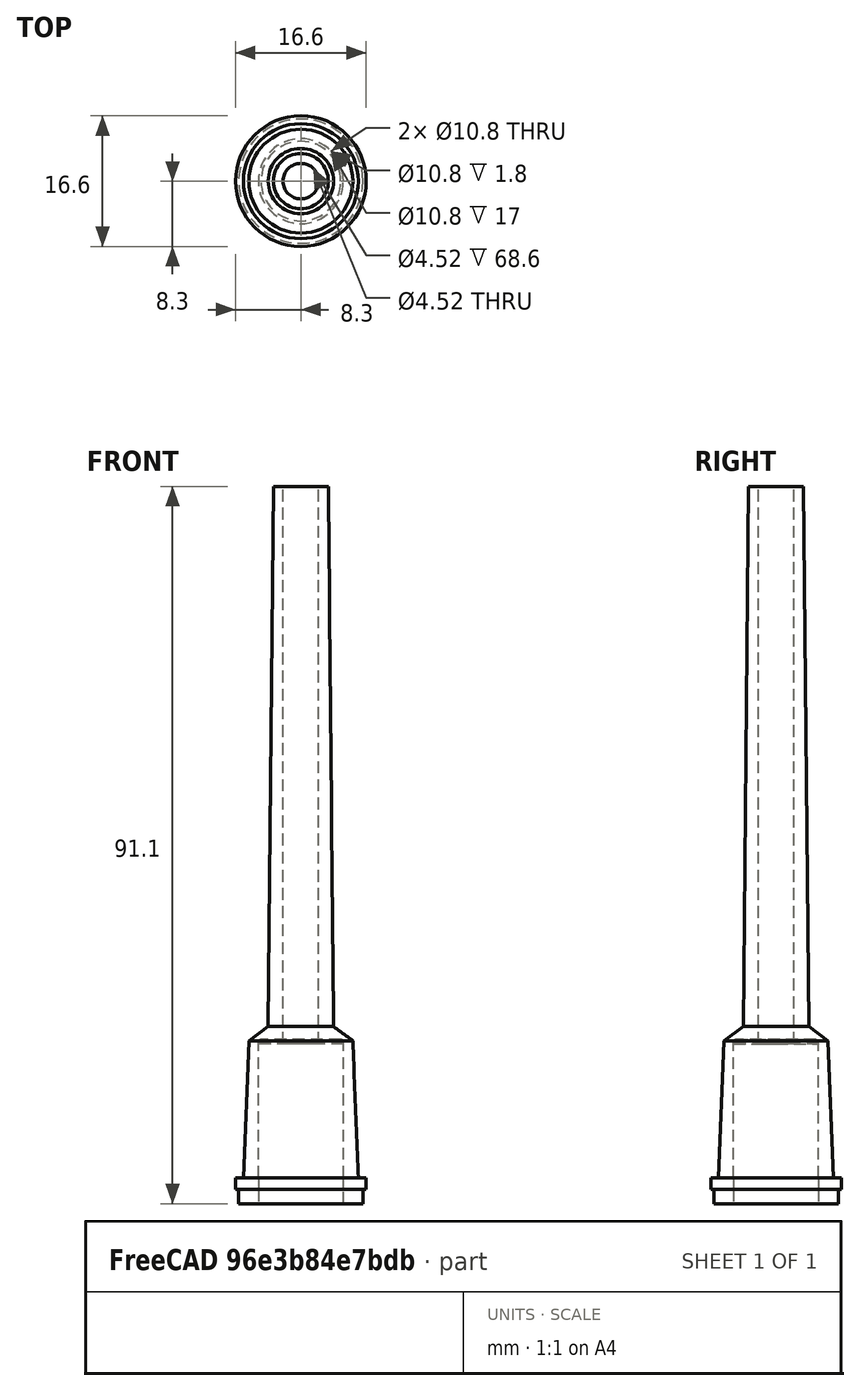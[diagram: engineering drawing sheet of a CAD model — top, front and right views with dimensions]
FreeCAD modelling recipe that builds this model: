
FCSTD DOCUMENT  (FreeCAD 0.19R17331 (Git))
Label: gilson_p200_vastago
License: All rights reserved
LicenseURL: http://en.wikipedia.org/wiki/All_rights_reserved
objects: Sketcher::SketchObject×9, PartDesign::AdditiveLoft×3, PartDesign::Pad×2, Spreadsheet::Sheet×1, App::FeaturePython×1, App::AnnotationLabel×1, PartDesign::Body×1
note: 20 computed .brp shape members not serialized (recipe doc carries the construction recipe); baked Part::Feature solids carry a one-line shape summary decoded from their .brp

FEATURE [Sketcher::SketchObject] Sketch  label="etapa1"
  MapMode = 5
  Support = -> [XY_Plane]
  expr: Constraints[3] = Spreadsheet.F2
  expr: Constraints[1] = Spreadsheet.B1
  sketch-geometry (2):
    g0: Circle CenterX=0 CenterY=0 CenterZ=0 NormalX=0 NormalY=0 NormalZ=1 AngleXU=0 Radius=7.9
    g1: Circle CenterX=0 CenterY=0 CenterZ=0 NormalX=0 NormalY=0 NormalZ=1 AngleXU=0 Radius=5.4
  constraints (4):
    c: Coincident(g0,g-1)
    c: Diameter(g0) = 15.8
    c: Coincident(g1,g0)
    c: Diameter(g1) = 10.8
FEATURE [PartDesign::Pad] Pad  label="etapa1pad"
  Length = 1.8
  Length2 = 100
  Profile = -> Sketch
  Type = 0
  expr: Length = Spreadsheet.B2
FEATURE [Spreadsheet::Sheet] Spreadsheet
  cells = A1=d1; B1=15.8; E1=h hueco interno; F1=20.3; A2=a1; B2=1.8; C2=cno reborde 45º; E2=d hueco interno; F2=10.8; G2=quizas 10.7; H2=parece ser cilindrico; E3=suma alturas externas; F3==B2 + B5 + B9 + B13; A4=d2; B4=16.6; A5=a2; B5=1.5; C5=altura cumul; D5==B2 + B5; G6=d piston; H6=4.02; A7=cono d1; B7=14.6; G7=tolerancia; H7==H6 + 0.5; A8=cono d2; B8=13.2; G8=h piston relajado; H8=49.2; A9=cono h; B9=17.4; C9=altura cumul; D9==D5 + B9; G9=desplazamiento max; H9==I9 - J9; I9=34.2; J9=14.8; G10=h piston maxima; H10==H8 + H9; A11=conito d1; B11==B8; A12=conito d2; B12=8.300000000000001; A13=conito h; B13=1.8; C13=altura cumul; D13==D9 + B13; A15=vastago h1; B15==90 - B18; C15=altura cumul; D15==D13 + B15; A16=vastago d1; B16==B12; A17=vastago d2; B17=5; C17=a la altura del desplazamiento maximo del piston es:; D17=7; A18=vastago h2; B18=0.8; A19=vastago d3; B19=4.5
FEATURE [Sketcher::SketchObject] Sketch001  label="etapa2"
  AttachmentOffset = pos=(0,0,1.8) rot=(0,0,1;0rad)
  MapMode = 5
  Placement = pos=(0,0,1.8) rot=(0,0,1;0rad)
  Support = -> [XY_Plane]
  expr: AttachmentOffset.Base.z = Spreadsheet.B2
  expr: Constraints[3] = Spreadsheet.F2
  expr: Constraints[1] = Spreadsheet.B4
  sketch-geometry (2):
    g0: Circle CenterX=0 CenterY=0 CenterZ=0 NormalX=0 NormalY=0 NormalZ=1 AngleXU=0 Radius=8.3
    g1: Circle CenterX=0 CenterY=0 CenterZ=0 NormalX=0 NormalY=0 NormalZ=1 AngleXU=0 Radius=5.4
  constraints (4):
    c: Coincident(g0,g-1)
    c: Diameter(g0) = 16.6
    c: Coincident(g1,g0)
    c: Diameter(g1) = 10.8
FEATURE [PartDesign::Pad] Pad001  label="etapa2pad"
  BaseFeature = -> Pad
  Length = 1.5
  Length2 = 100
  Profile = -> Sketch001
  Type = 0
  expr: Length = Spreadsheet.B5
FEATURE [Sketcher::SketchObject] Sketch002  label="etapa3_001"
  AttachmentOffset = pos=(0,0,3.3) rot=(0,0,1;0rad)
  MapMode = 5
  Placement = pos=(0,0,3.3) rot=(0,0,1;0rad)
  Support = -> [XY_Plane]
  expr: AttachmentOffset.Base.z = Spreadsheet.D5
  expr: Constraints[3] = Spreadsheet.B7
  expr: Constraints[2] = Spreadsheet.F2
  sketch-geometry (2):
    g0: Circle CenterX=0 CenterY=0 CenterZ=0 NormalX=0 NormalY=0 NormalZ=1 AngleXU=0 Radius=5.4
    g1: Circle CenterX=0 CenterY=0 CenterZ=0 NormalX=0 NormalY=0 NormalZ=1 AngleXU=0 Radius=7.3
  constraints (4):
    c: Coincident(g0,g-1)
    c: Coincident(g1,g0)
    c: Diameter(g0) = 10.8
    c: Diameter(g1) = 14.6
FEATURE [Sketcher::SketchObject] Sketch003  label="etapa3_002"
  AttachmentOffset = pos=(0,0,20.7) rot=(0,0,1;0rad)
  MapMode = 5
  Placement = pos=(0,0,20.7) rot=(0,0,1;0rad)
  Support = -> [XY_Plane]
  expr: AttachmentOffset.Base.z = Spreadsheet.D9
  expr: Constraints[3] = Spreadsheet.B8
  expr: Constraints[2] = Spreadsheet.F2
  sketch-geometry (2):
    g0: Circle CenterX=0 CenterY=0 CenterZ=0 NormalX=0 NormalY=0 NormalZ=1 AngleXU=0 Radius=5.4
    g1: Circle CenterX=0 CenterY=0 CenterZ=0 NormalX=0 NormalY=0 NormalZ=1 AngleXU=0 Radius=6.6
  constraints (4):
    c: Coincident(g0,g-1)
    c: Coincident(g1,g0)
    c: Diameter(g0) = 10.8
    c: Diameter(g1) = 13.2
FEATURE [Sketcher::SketchObject] Sketch004
  AttachmentOffset = pos=(0,0,20.3) rot=(0,0,1;0rad)
  MapMode = 5
  Placement = pos=(0,0,20.3) rot=(0,0,1;0rad)
  Support = -> [XY_Plane]
  expr: Constraints[3] = Spreadsheet.F2
  expr: AttachmentOffset.Base.z = Spreadsheet.F1
  expr: Constraints[2] = Spreadsheet.H7
  sketch-geometry (2):
    g0: Circle CenterX=0 CenterY=0 CenterZ=0 NormalX=0 NormalY=0 NormalZ=1 AngleXU=0 Radius=2.26
    g1: Circle CenterX=0 CenterY=0 CenterZ=0 NormalX=0 NormalY=0 NormalZ=1 AngleXU=0 Radius=5.4
  constraints (4):
    c: Coincident(g0,g-1)
    c: Coincident(g1,g0)
    c: Diameter(g0) = 4.52
    c: Diameter(g1) = 10.8
FEATURE [Sketcher::SketchObject] Sketch005  label="etapa4_conito"
  AttachmentOffset = pos=(0,0,22.5) rot=(0,0,1;0rad)
  MapMode = 5
  Placement = pos=(0,0,22.5) rot=(0,0,1;0rad)
  Support = -> [XY_Plane]
  expr: Constraints[2] = Spreadsheet.H7
  expr: Constraints[3] = Spreadsheet.B12
  expr: AttachmentOffset.Base.z = Spreadsheet.D13
  sketch-geometry (2):
    g0: Circle CenterX=0 CenterY=0 CenterZ=0 NormalX=0 NormalY=0 NormalZ=1 AngleXU=0 Radius=2.26
    g1: Circle CenterX=0 CenterY=0 CenterZ=0 NormalX=0 NormalY=0 NormalZ=1 AngleXU=0 Radius=4.15
  constraints (4):
    c: Coincident(g0,g-1)
    c: Coincident(g1,g0)
    c: Diameter(g0) = 4.52
    c: Diameter(g1) = 8.3
FEATURE [PartDesign::AdditiveLoft] AdditiveLoft
  BaseFeature = -> Pad001
  Closed = false
  Profile = -> Sketch002
  Ruled = true
  Sections = -> [Sketch003,Sketch005]
FEATURE [Sketcher::SketchObject] Sketch006  label="etapa4_conito001"
  AttachmentOffset = pos=(0,0,22.5) rot=(0,0,1;0rad)
  MapMode = 5
  Placement = pos=(0,0,22.5) rot=(0,0,1;0rad)
  Support = -> [XY_Plane]
  expr: Constraints[2] = Spreadsheet.H7
  expr: Constraints[3] = Spreadsheet.B12
  expr: AttachmentOffset.Base.z = Spreadsheet.D13
  sketch-geometry (2):
    g0: Circle CenterX=0 CenterY=0 CenterZ=0 NormalX=0 NormalY=0 NormalZ=1 AngleXU=0 Radius=2.26
    g1: Circle CenterX=0 CenterY=0 CenterZ=0 NormalX=0 NormalY=0 NormalZ=1 AngleXU=0 Radius=4.15
  constraints (4):
    c: Coincident(g0,g-1)
    c: Coincident(g1,g0)
    c: Diameter(g0) = 4.52
    c: Diameter(g1) = 8.3
FEATURE [PartDesign::AdditiveLoft] AdditiveLoft001
  BaseFeature = -> AdditiveLoft
  Closed = false
  Profile = -> Sketch004
  Ruled = false
  Sections = -> [Sketch006]
FEATURE [App::FeaturePython] Dimension  label="Distance"  # Draft dimension (typed FeaturePython)
  Diameter = false
  Dimline = (0,0,11.25)
  Direction = (0,0,0)
  Distance = 22.5
  End = (0,0,22.5)
  Normal = (0,0,-1)
  Start = (0,0,0)
FEATURE [App::AnnotationLabel] DistanceLbl
  BasePosition = (0,0,11.25)
  LabelText = ds: 22.5 mm | dx: 0.0 | dy: 0.0 | dz: 22.5
  TextPosition = (0,0,0)
FEATURE [Sketcher::SketchObject] Sketch007  label="etapa4_vastago002"
  AttachmentOffset = pos=(0,0,91.1) rot=(0,0,1;0rad)
  MapMode = 5
  Placement = pos=(0,0,91.1) rot=(0,0,1;0rad)
  Support = -> [XY_Plane]
  expr: Constraints[2] = Spreadsheet.H7
  expr: Constraints[3] = Spreadsheet.D17
  expr: AttachmentOffset.Base.z = Spreadsheet.D13 + Spreadsheet.H10
  sketch-geometry (2):
    g0: Circle CenterX=0 CenterY=0 CenterZ=0 NormalX=0 NormalY=0 NormalZ=1 AngleXU=0 Radius=2.26
    g1: Circle CenterX=0 CenterY=0 CenterZ=0 NormalX=0 NormalY=0 NormalZ=1 AngleXU=0 Radius=3.5
  constraints (4):
    c: Coincident(g0,g-1)
    c: Coincident(g1,g0)
    c: Diameter(g0) = 4.52
    c: Diameter(g1) = 7
FEATURE [Sketcher::SketchObject] Sketch008  label="etapa4_vastago001"
  AttachmentOffset = pos=(0,0,22.5) rot=(0,0,1;0rad)
  MapMode = 5
  Placement = pos=(0,0,22.5) rot=(0,0,1;0rad)
  Support = -> [XY_Plane]
  expr: Constraints[2] = Spreadsheet.H7
  expr: Constraints[3] = Spreadsheet.B12
  expr: AttachmentOffset.Base.z = Spreadsheet.D13
  sketch-geometry (2):
    g0: Circle CenterX=0 CenterY=0 CenterZ=0 NormalX=0 NormalY=0 NormalZ=1 AngleXU=0 Radius=2.26
    g1: Circle CenterX=0 CenterY=0 CenterZ=0 NormalX=0 NormalY=0 NormalZ=1 AngleXU=0 Radius=4.15
  constraints (4):
    c: Coincident(g0,g-1)
    c: Coincident(g1,g0)
    c: Diameter(g0) = 4.52
    c: Diameter(g1) = 8.3
FEATURE [PartDesign::AdditiveLoft] AdditiveLoft002  label="Vastago_minimo"
  BaseFeature = -> AdditiveLoft001
  Closed = false
  Profile = -> Sketch008
  Ruled = false
  Sections = -> [Sketch007]
FEATURE [PartDesign::Body] Body  label="vastago_p200"
  Group = -> [Sketch,Pad,Sketch001,Pad001,Sketch002,Sketch003,Sketch004,Sketch005,AdditiveLoft,Sketch006,AdditiveLoft001,Sketch007,Sketch008,AdditiveLoft002]
  Origin = -> Origin
  Tip = -> AdditiveLoft002
